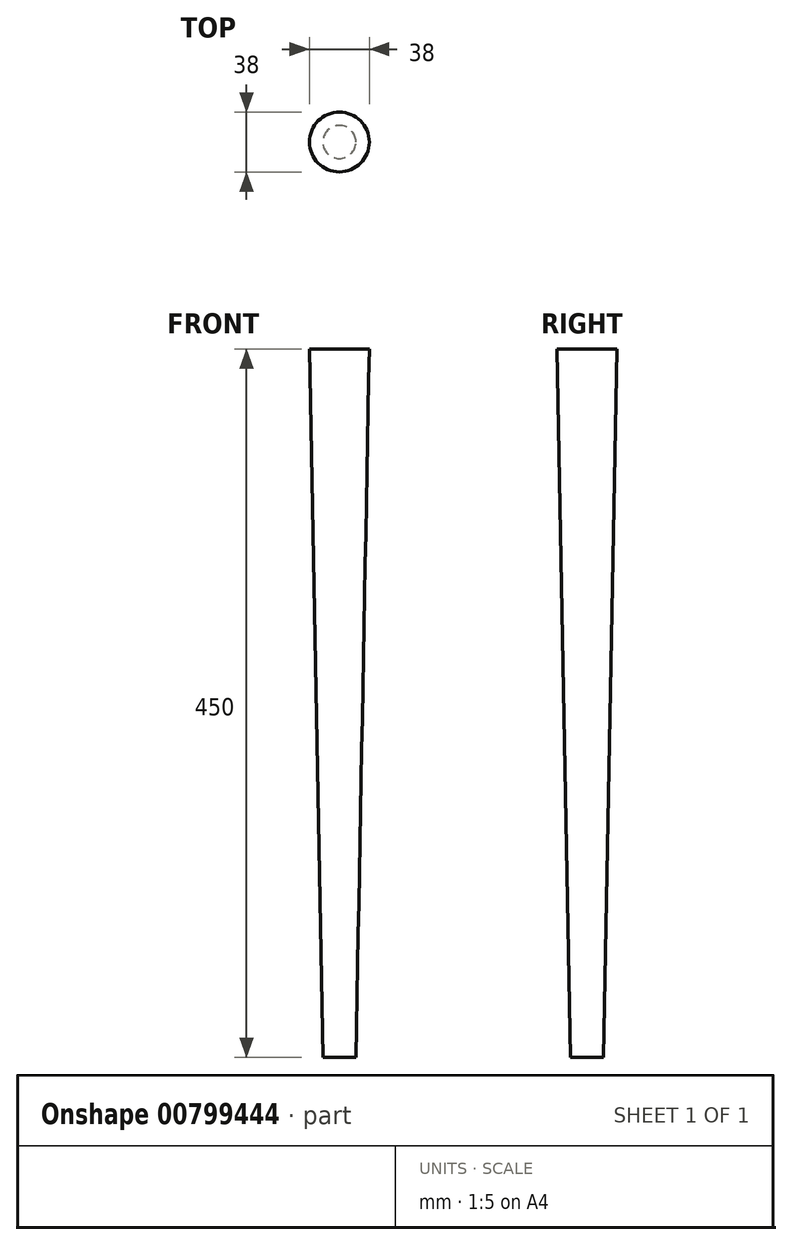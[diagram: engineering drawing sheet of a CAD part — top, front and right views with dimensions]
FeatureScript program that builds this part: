
annotation { "Feature Type Name" : "Feature", "Feature Type Description" : "" }
export const myFeature = defineFeature(function(context is Context, id is Id, definition is map)
    precondition{}
    {
        {
            var Q0;
            Q0=qCreatedBy(makeId("Top.planeOp"),FACE);
            var sketch = newSketch(context, id + "F0", { "sketchPlane" : qUnion([Q0])});
            skCircle(sketch, "E0", {"center": v(0, 0) * mm, "radius": 10.5 * mm});
            skSolve(sketch);
        }
        {
            var Q0;
            Q0=qCreatedBy(makeId("Top.planeOp"),FACE);
            cPlane(context, id + "F1", {"entities" : qUnion([Q0]), "cplaneType" : CPlaneType.OFFSET, "offset" : 450 * mm, "width" : 150 * mm, "height" : 150 * mm});
        }
        {
            var Q0;
            Q0=qCreatedBy(id+"F1.planeOp",FACE);
            var sketch = newSketch(context, id + "F2", { "sketchPlane" : qUnion([Q0])});
            skCircle(sketch, "E1", {"center": v(0, 0) * mm, "radius": 19 * mm});
            skSolve(sketch);
        }
        {
            var Q0;
            Q0=makeQuery(id+"F2.imprint","IMPRINT",FACE,{"disambiguationData":[TD([[makeQuery(id+"F2.imprint","IMPRINT",EDGE,{"derivedFrom":sQuery(id+"F2.wireOp",EDGE,"E1")}),1.0]])]});
            var Q1;
            Q1=makeQuery(id+"F0.imprint","IMPRINT",FACE,{"disambiguationData":[TD([[makeQuery(id+"F0.imprint","IMPRINT",EDGE,{"derivedFrom":sQuery(id+"F0.wireOp",EDGE,"E0")}),1.0]])]});
            loft(context, id + "F3", {"sheetProfilesArray" : [{ "sheetProfileEntities" : qUnion([Q0]) }, { "sheetProfileEntities" : qUnion([Q1]) }]});
        }
        {
            var Q0;
            Q0=makeQuery(id+"F3.opLoft","CAP_FACE",FACE,{"disambiguationData":[OSD([makeQuery(id+"F2.imprint","IMPRINT",FACE,{"disambiguationData":[TD([[makeQuery(id+"F2.imprint","IMPRINT",EDGE,{"derivedFrom":sQuery(id+"F2.wireOp",EDGE,"E1")}),1.0]])]})])],"isStart":true});
            var sketch = newSketch(context, id + "F4", { "sketchPlane" : qUnion([Q0])});
            skLineSegment(sketch, "E2", {"start": v(0, 0) * mm, "end": v(0, -19) * mm});
            skSolve(sketch);
        }
        {
            var Q0;
            Q0=qCreatedBy(id+"F1.planeOp",FACE);
            var Q1;
            Q1=sQuery(id+"F4.wireOp",EDGE,"E2");
            cPlane(context, id + "F5", {"entities" : qUnion([Q0, Q1]), "cplaneType" : CPlaneType.LINE_ANGLE, "offset" : 25 * mm, "angle" : 10 * degree, "width" : 150 * mm, "height" : 150 * mm});
        }
        {
            var Q0;
            Q0=makeQuery(id+"F4.imprint","IMPRINT",FACE,{"disambiguationData":[TD([[makeQuery(id+"F4.imprint","IMPRINT",EDGE,{"derivedFrom":makeQuery(id+"F3.opLoft","MID_CAP_EDGE",EDGE,{"disambiguationData":[OSD([sQuery(id+"F2.wireOp",EDGE,"E1")])],"capPos":0.0})}),-1.0]])]});
            var sketch = newSketch(context, id + "F6", { "sketchPlane" : qUnion([Q0])});
            skLineSegment(sketch, "E3.bottom", {"start": v(19, -19) * mm, "end": v(-19, -19) * mm});
            skLineSegment(sketch, "E3.top", {"start": v(19, 19) * mm, "end": v(-19, 19) * mm});
            skLineSegment(sketch, "E3.left", {"start": v(19, -19) * mm, "end": v(19, 19) * mm});
            skLineSegment(sketch, "E3.right", {"start": v(-19, -19) * mm, "end": v(-19, 19) * mm});
            skPoint(sketch, "E3.middle", {"position": v(0, 0) * mm});
            skSolve(sketch);
        }
    });
